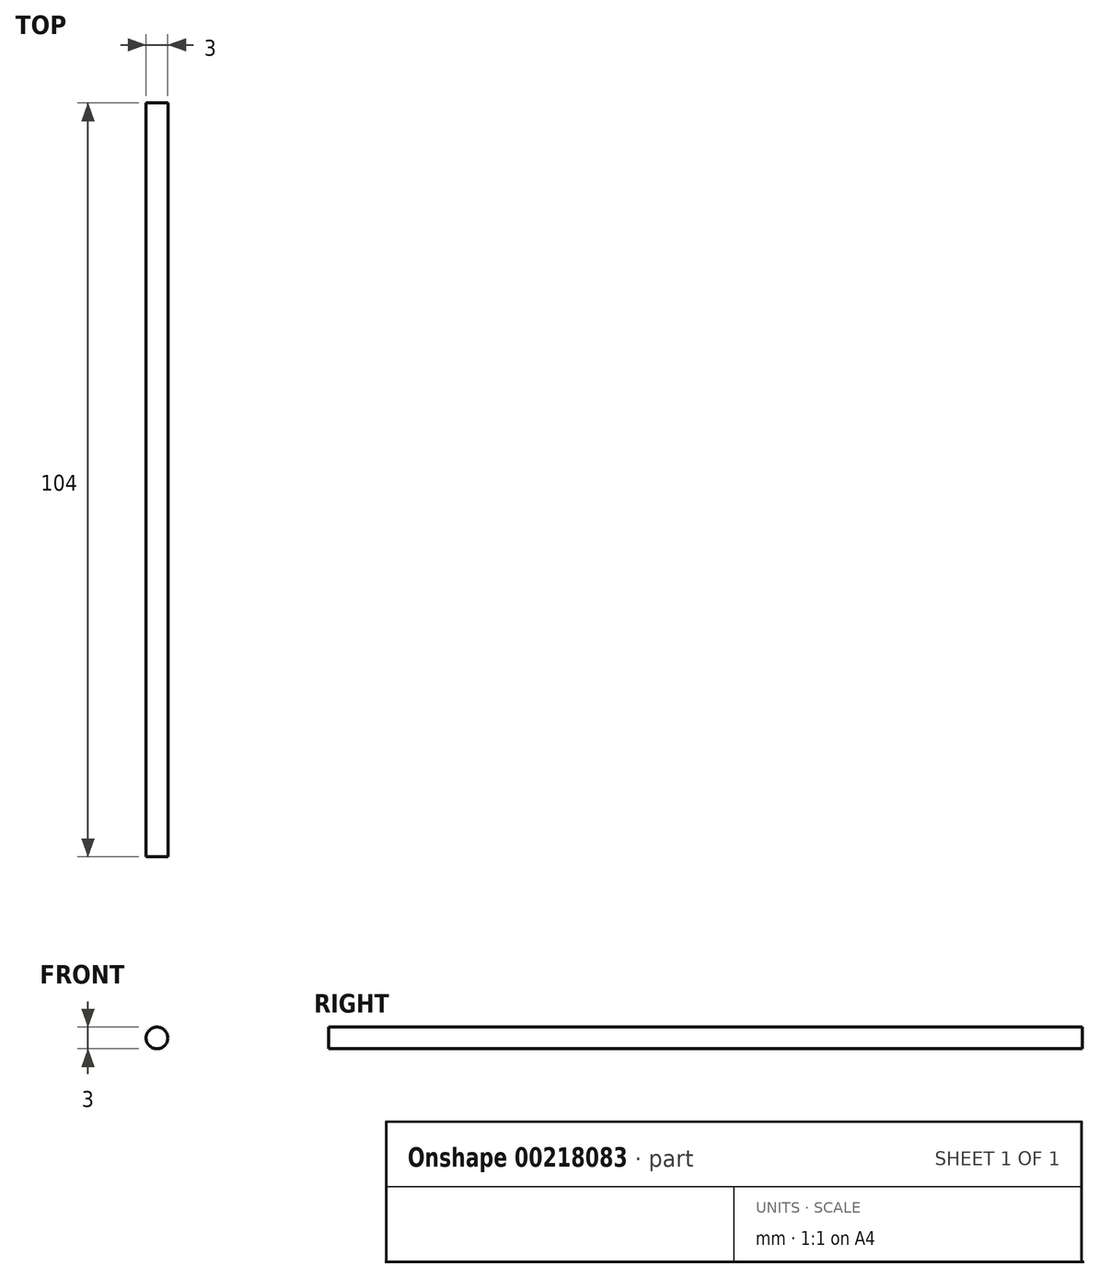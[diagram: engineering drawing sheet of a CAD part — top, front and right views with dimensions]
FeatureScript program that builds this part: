
annotation { "Feature Type Name" : "Feature", "Feature Type Description" : "" }
export const myFeature = defineFeature(function(context is Context, id is Id, definition is map)
    precondition{}
    {
        {
            var Q0;
            Q0=qCreatedBy(makeId("Front.planeOp"),FACE);
            var sketch = newSketch(context, id + "F0", { "sketchPlane" : qUnion([Q0])});
            skCircle(sketch, "E0", {"center": v(18.68, 12.5) * mm, "radius": 1.5 * mm});
            skSolve(sketch);
        }
        {
            var Q0;
            Q0=makeQuery(id+"F0.imprint","IMPRINT",FACE,{"disambiguationData":[TD([[makeQuery(id+"F0.imprint","IMPRINT",EDGE,{"derivedFrom":sQuery(id+"F0.wireOp",EDGE,"E0")}),1.0]])]});
            extrude(context, id + "F1", {"entities" : qUnion([Q0]), "depth" : 104 * mm});
        }
    });
